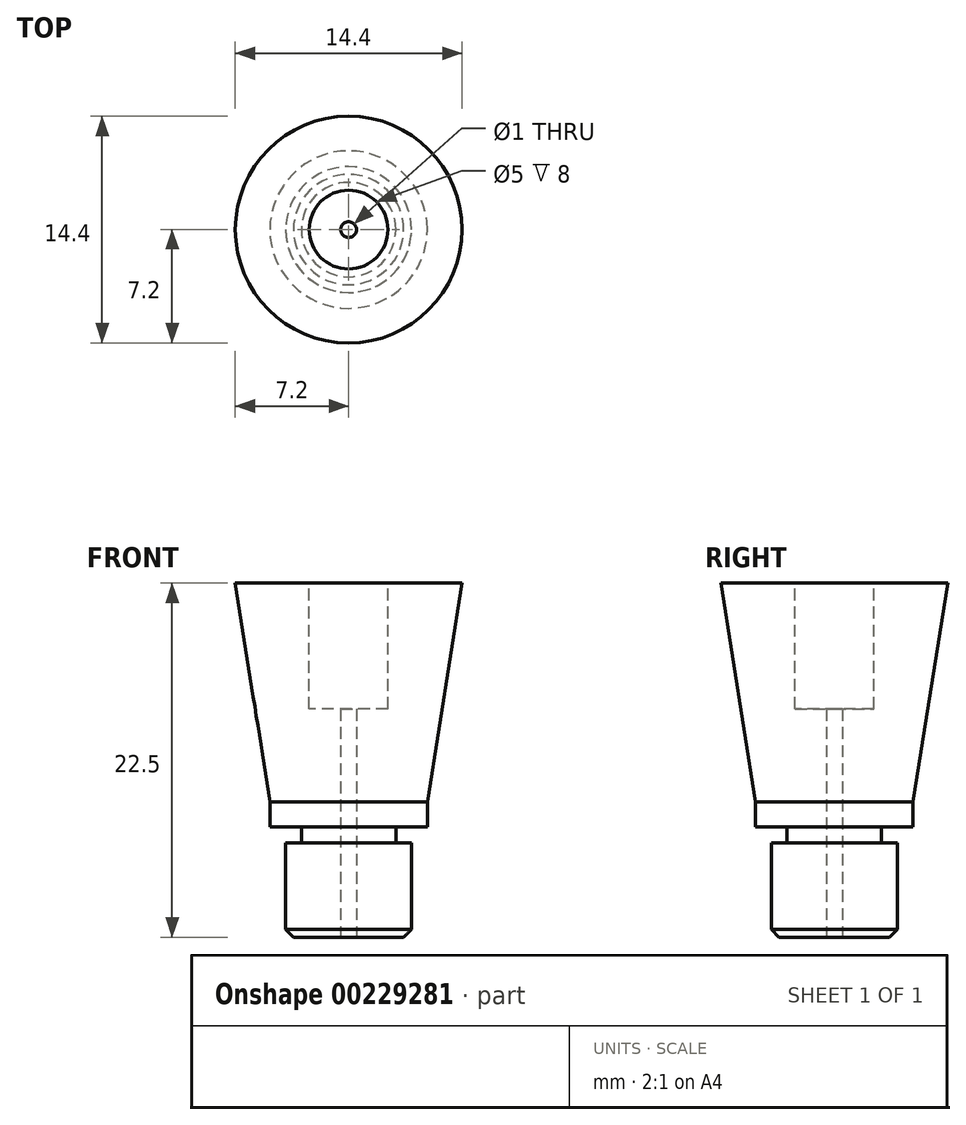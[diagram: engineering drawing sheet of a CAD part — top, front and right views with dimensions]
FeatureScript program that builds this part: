
annotation { "Feature Type Name" : "Feature", "Feature Type Description" : "" }
export const myFeature = defineFeature(function(context is Context, id is Id, definition is map)
    precondition{}
    {
        {
            var Q0;
            Q0=qCreatedBy(makeId("Front.planeOp"),FACE);
            var sketch = newSketch(context, id + "F0", { "sketchPlane" : qUnion([Q0])});
            skLineSegment(sketch, "E0", {"start": v(0, 22.5) * mm, "end": v(-7.2, 22.5) * mm});
            skLineSegment(sketch, "E1", {"start": v(-7.2, 22.5) * mm, "end": v(-5, 8.6) * mm});
            skLineSegment(sketch, "E2", {"start": v(-5, 8.6) * mm, "end": v(-5, 7) * mm});
            skLineSegment(sketch, "E3", {"start": v(-5, 7) * mm, "end": v(-3, 7) * mm});
            skLineSegment(sketch, "E4", {"start": v(-3, 7) * mm, "end": v(-3, 6) * mm});
            skLineSegment(sketch, "E5", {"start": v(-3, 6) * mm, "end": v(-4, 6) * mm});
            skLineSegment(sketch, "E6", {"start": v(-4, 6) * mm, "end": v(-4, 0) * mm});
            skLineSegment(sketch, "E7", {"start": v(-4, 0) * mm, "end": v(0, 0) * mm});
            skLineSegment(sketch, "E8", {"start": v(0, 0) * mm, "end": v(0, 22.5) * mm});
            skSolve(sketch);
        }
        {
            var Q0;
            Q0=makeQuery(id+"F0.imprint","IMPRINT",FACE,{"disambiguationData":[TD([[makeQuery(id+"F0.imprint","IMPRINT",EDGE,{"derivedFrom":sQuery(id+"F0.wireOp",EDGE,"E0")}),1.0]])]});
            var Q1;
            Q1=sQuery(id+"F0.wireOp",EDGE,"E8");
            revolve(context, id + "F1", {"entities" : qUnion([Q0]), "axis" : qUnion([Q1]), "revolveType" : RevolveType.FULL});
        }
        {
            var Q0;
            Q0=qCreatedBy(makeId("Top.planeOp"),FACE);
            var sketch = newSketch(context, id + "F2", { "sketchPlane" : qUnion([Q0])});
            skCircle(sketch, "E9", {"center": v(0, 0) * mm, "radius": 0.5 * mm});
            skSolve(sketch);
        }
        {
            var Q0;
            Q0 = qSketchRegion(id + "F2", true);
            extrude(context, id + "F3", {"entities" : qUnion([Q0]), "operationType" : NewBodyOperationType.REMOVE, "depth" : 25 * mm});
        }
        {
            var Q0;
            Q0=makeQuery(id+"F1.opRevolve","SWEPT_FACE",FACE,{"disambiguationData":[OSD([sQuery(id+"F0.wireOp",EDGE,"E0")])]});
            var sketch = newSketch(context, id + "F4", { "sketchPlane" : qUnion([Q0])});
            skCircle(sketch, "E10", {"center": v(0, 0) * mm, "radius": 2.5 * mm});
            skSolve(sketch);
        }
        {
            var Q0;
            Q0=makeQuery(id+"F4.imprint","IMPRINT",FACE,{"disambiguationData":[TD([[makeQuery(id+"F4.imprint","IMPRINT",EDGE,{"derivedFrom":sQuery(id+"F4.wireOp",EDGE,"E10")}),1.0]])]});
            extrude(context, id + "F5", {"entities" : qUnion([Q0]), "operationType" : NewBodyOperationType.REMOVE, "oppositeDirection" : true, "depth" : 8 * mm});
        }
        {
            var Q0;
            Q0=makeQuery(id+"F1.opRevolve","SWEPT_EDGE",EDGE,{"disambiguationData":[OSD([sQuery(id+"F0.wireOp",EDGE,"E6"),sQuery(id+"F0.wireOp",EDGE,"E7")])]});
            chamfer(context, id + "F6", {"entities" : qUnion([Q0]), "width" : 0.5 * mm, "tangentPropagation" : true});
        }
    });
